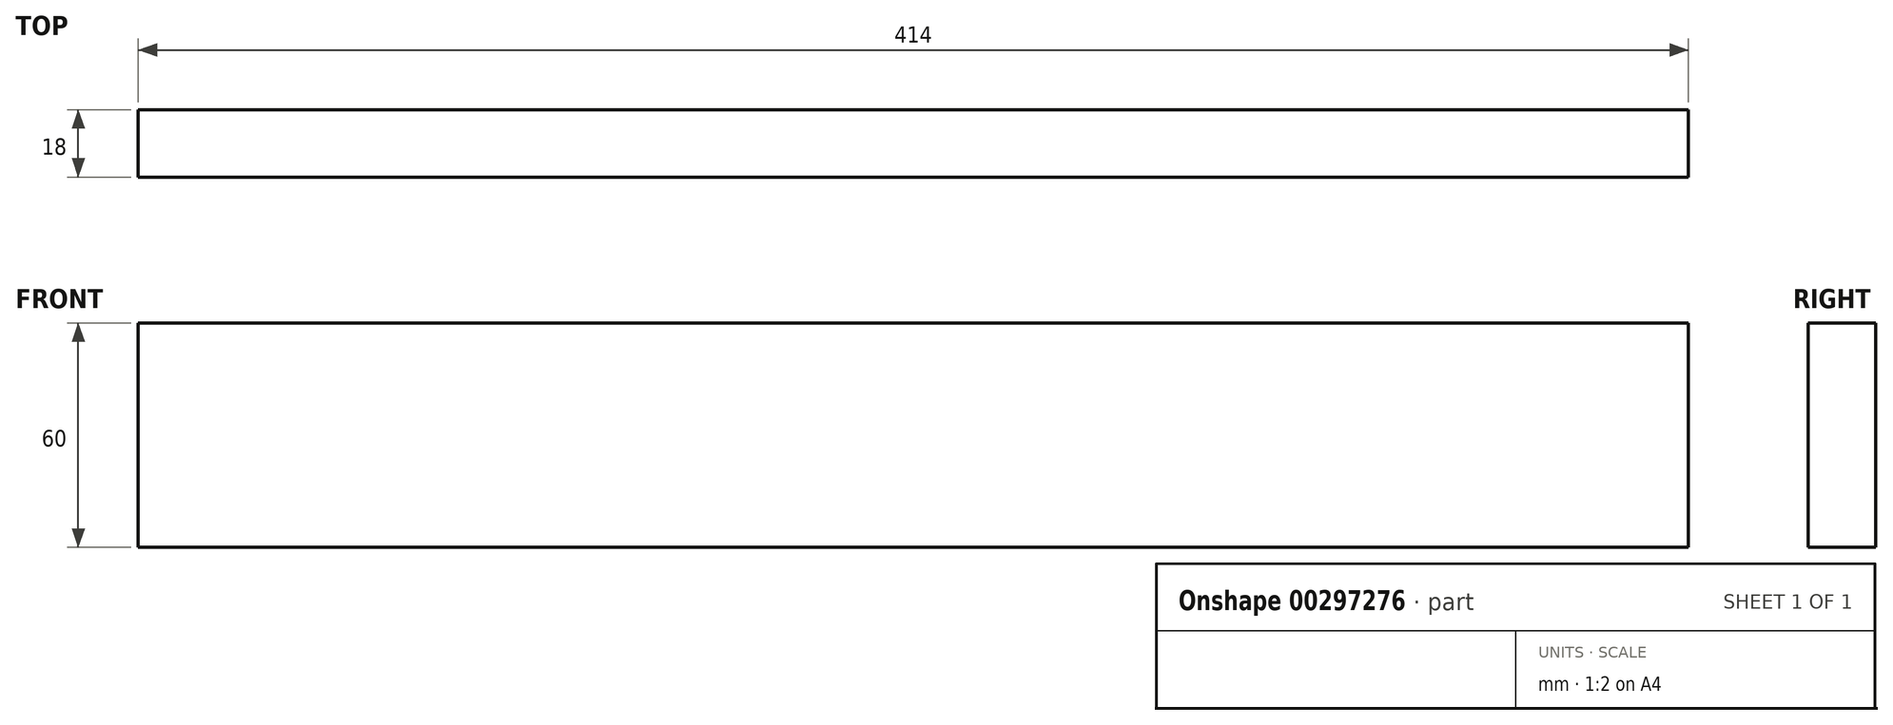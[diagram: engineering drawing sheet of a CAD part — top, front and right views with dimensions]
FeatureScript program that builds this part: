
annotation { "Feature Type Name" : "Feature", "Feature Type Description" : "" }
export const myFeature = defineFeature(function(context is Context, id is Id, definition is map)
    precondition{}
    {
        {
            var Q0;
            Q0=qCreatedBy(makeId("Right.planeOp"),FACE);
            var sketch = newSketch(context, id + "F0", { "sketchPlane" : qUnion([Q0])});
            skLineSegment(sketch, "E0.bottom", {"start": v(9, 30) * mm, "end": v(-9, 30) * mm});
            skLineSegment(sketch, "E0.top", {"start": v(9, -30) * mm, "end": v(-9, -30) * mm});
            skLineSegment(sketch, "E0.left", {"start": v(9, 30) * mm, "end": v(9, -30) * mm});
            skLineSegment(sketch, "E0.right", {"start": v(-9, 30) * mm, "end": v(-9, -30) * mm});
            skPoint(sketch, "E0.middle", {"position": v(0, 0) * mm});
            skSolve(sketch);
        }
        {
            var Q0;
            Q0 = qSketchRegion(id + "F0", true);
            extrude(context, id + "F1", {"entities" : qUnion([Q0]), "depth" : 414 * mm});
        }
    });
